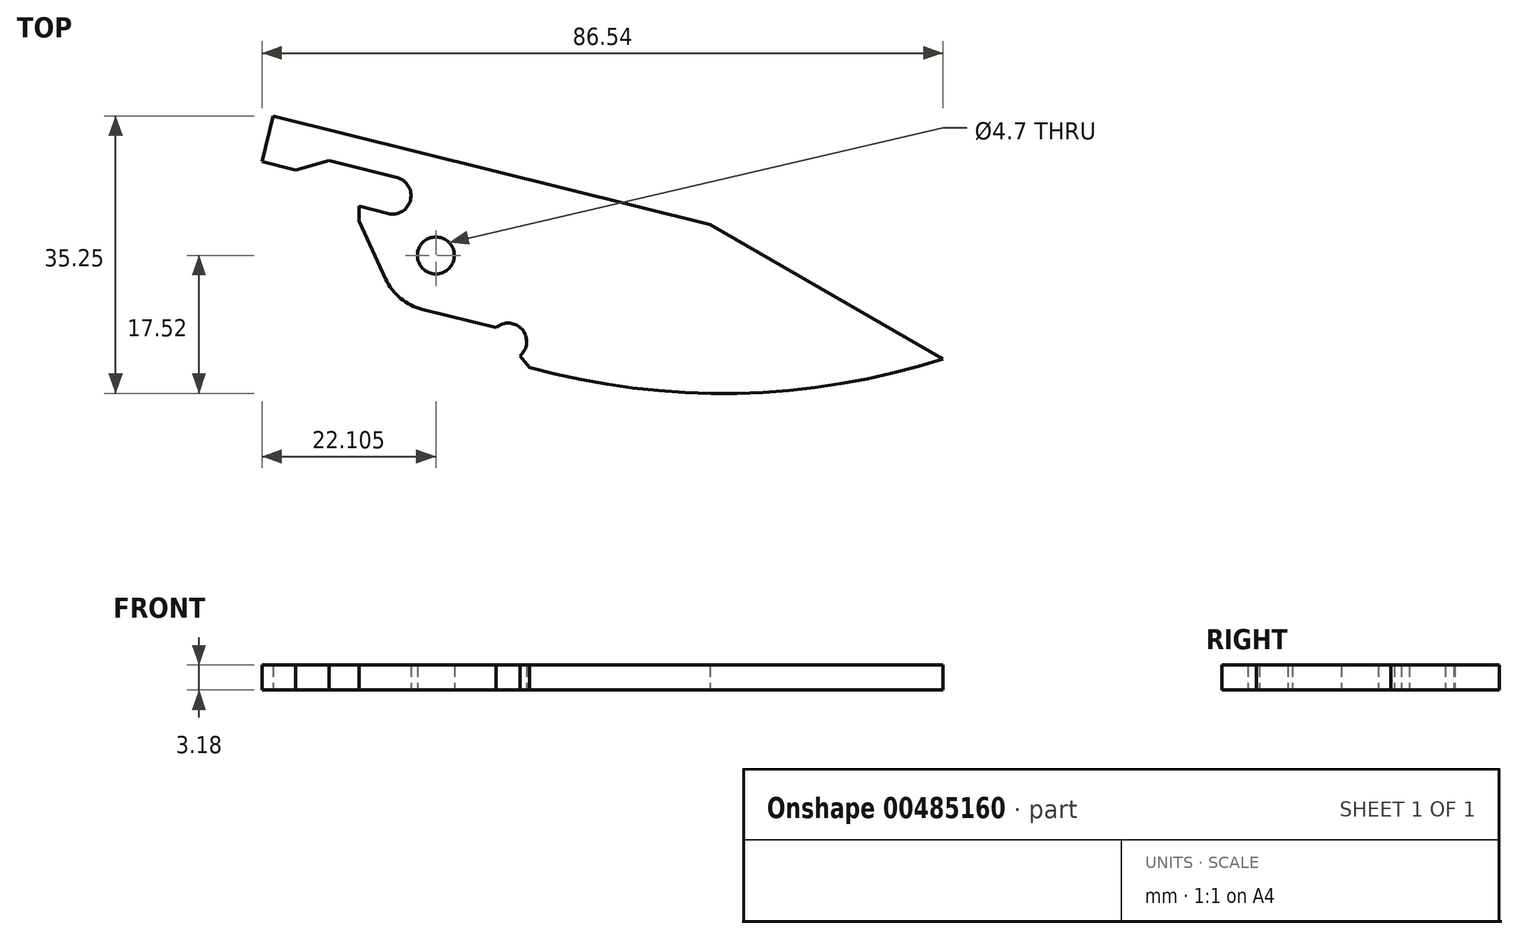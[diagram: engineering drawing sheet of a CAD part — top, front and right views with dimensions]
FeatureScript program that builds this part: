
annotation { "Feature Type Name" : "Feature", "Feature Type Description" : "" }
export const myFeature = defineFeature(function(context is Context, id is Id, definition is map)
    precondition{}
    {
        {
            var Q0;
            Q0=qCreatedBy(makeId("Top.planeOp"),FACE);
            var sketch = newSketch(context, id + "F0", { "sketchPlane" : qUnion([Q0])});
            skLineSegment(sketch, "E0.bottom", {"start": v(0, 0) * mm, "end": v(-69.85, 0) * mm, "construction": true});
            skLineSegment(sketch, "E0.top", {"start": v(0, 38.1) * mm, "end": v(-95.25, 38.1) * mm, "construction": true});
            skLineSegment(sketch, "E0.left", {"start": v(0, 0) * mm, "end": v(0, 38.1) * mm, "construction": true});
            skLineSegment(sketch, "E1", {"start": v(-69.85, 0) * mm, "end": v(-95.25, 38.1) * mm, "construction": true});
            skCircle(sketch, "E2", {"center": v(-66.68, 19.05) * mm, "radius": 2.35 * mm});
            skLineSegment(sketch, "E3", {"start": v(-75.86, 30) * mm, "end": v(-57.5, 8.1) * mm, "construction": true});
            skArc(sketch, "E4", {"start": v(-55.98, 6.3) * mm, "mid": v(-55.7, 9.62) * mm, "end": v(-59, 9.9) * mm});
            skArc(sketch, "E5", {"start": v(-73.07, 16.09) * mm, "mid": v(-71.16, 13.6) * mm, "end": v(-68.36, 12.2) * mm});
            skArc(sketch, "E6", {"start": v(-72.76, 24.38) * mm, "mid": v(-69.91, 26.1) * mm, "end": v(-71.62, 28.94) * mm});
            skLineSegment(sketch, "E7", {"start": v(-71.62, 28.94) * mm, "end": v(-80.25, 31.09) * mm});
            skLineSegment(sketch, "E8", {"start": v(-72.76, 24.38) * mm, "end": v(-76.46, 25.3) * mm});
            skLineSegment(sketch, "E9", {"start": v(-80.25, 31.09) * mm, "end": v(-84.47, 29.92) * mm});
            skLineSegment(sketch, "E10", {"start": v(-84.47, 29.92) * mm, "end": v(-88.78, 31) * mm});
            skLineSegment(sketch, "E11", {"start": v(-88.78, 31) * mm, "end": v(-87.34, 36.78) * mm});
            skLineSegment(sketch, "E12", {"start": v(-87.34, 36.78) * mm, "end": v(-31.88, 22.96) * mm});
            skLineSegment(sketch, "E13", {"start": v(-76.46, 25.3) * mm, "end": v(-76.46, 23.4) * mm});
            skLineSegment(sketch, "E14", {"start": v(-76.46, 25.3) * mm, "end": v(-85.08, 27.45) * mm, "construction": true});
            skLineSegment(sketch, "E15", {"start": v(-84.47, 29.92) * mm, "end": v(-85.08, 27.45) * mm, "construction": true});
            skCircle(sketch, "E16", {"center": v(-66.68, 19.05) * mm, "radius": 11.94 * mm, "construction": true});
            skLineSegment(sketch, "E17", {"start": v(-76.46, 23.4) * mm, "end": v(-73.07, 16.09) * mm});
            skLineSegment(sketch, "E18", {"start": v(-55.98, 6.3) * mm, "end": v(-54.76, 4.85) * mm});
            skLineSegment(sketch, "E19", {"start": v(-68.36, 12.2) * mm, "end": v(-59, 9.9) * mm});
            skLineSegment(sketch, "E20", {"start": v(-31.88, 22.96) * mm, "end": v(-2.24, 5.9) * mm});
            skArc(sketch, "E21", {"start": v(-54.76, 4.85) * mm, "mid": v(-28.42, 1.54) * mm, "end": v(-2.24, 5.9) * mm});
            skSolve(sketch);
        }
        {
            var Q0;
            Q0=makeQuery(id+"F0.imprint","IMPRINT",FACE,{"disambiguationData":[TD([[makeQuery(id+"F0.imprint","IMPRINT",EDGE,{"derivedFrom":sQuery(id+"F0.wireOp",EDGE,"E2")}),-1.0]])]});
            extrude(context, id + "F1", {"entities" : qUnion([Q0]), "depth" : 3.17 * mm});
        }
    });
